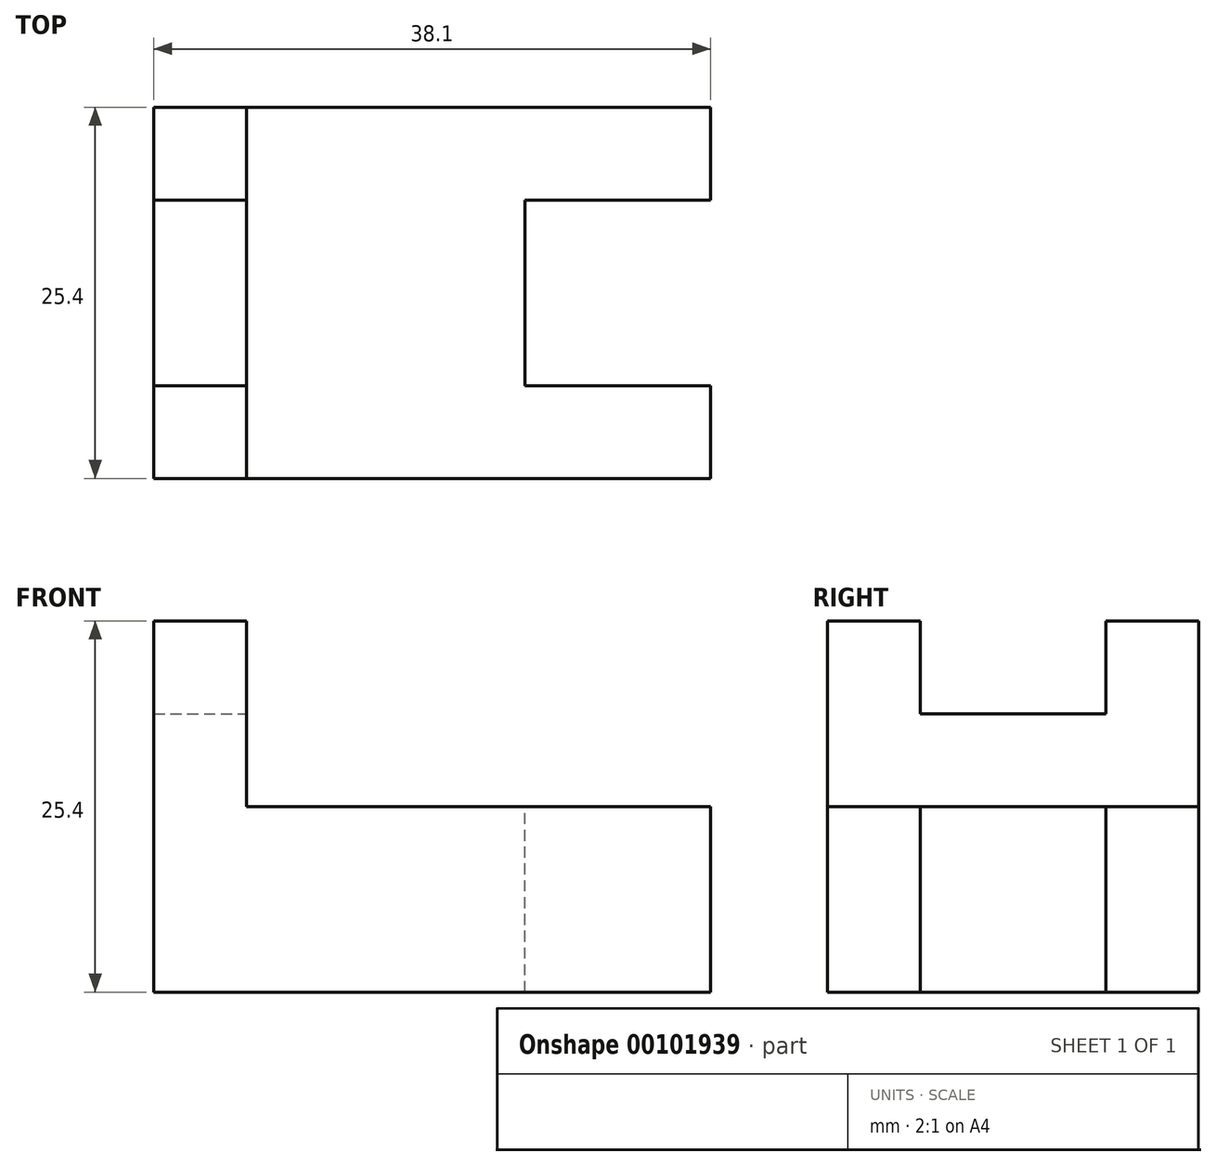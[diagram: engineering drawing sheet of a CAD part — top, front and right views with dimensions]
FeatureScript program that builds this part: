
annotation { "Feature Type Name" : "Feature", "Feature Type Description" : "" }
export const myFeature = defineFeature(function(context is Context, id is Id, definition is map)
    precondition{}
    {
        {
            var Q0;
            Q0=qCreatedBy(makeId("Front.planeOp"),FACE);
            var sketch = newSketch(context, id + "F0", { "sketchPlane" : qUnion([Q0])});
            skLineSegment(sketch, "E0", {"start": v(0, 0) * mm, "end": v(38.1, 0) * mm});
            skLineSegment(sketch, "E1", {"start": v(38.1, 0) * mm, "end": v(38.1, 12.7) * mm});
            skLineSegment(sketch, "E2", {"start": v(38.1, 12.7) * mm, "end": v(6.35, 12.7) * mm});
            skLineSegment(sketch, "E3", {"start": v(6.35, 12.7) * mm, "end": v(6.35, 25.4) * mm});
            skLineSegment(sketch, "E4", {"start": v(6.35, 25.4) * mm, "end": v(0, 25.4) * mm});
            skLineSegment(sketch, "E5", {"start": v(0, 25.4) * mm, "end": v(0, 0) * mm});
            skSolve(sketch);
        }
        {
            var Q0;
            Q0 = qSketchRegion(id + "F0", true);
            extrude(context, id + "F1", {"entities" : qUnion([Q0]), "endBound" : BoundingType.SYMMETRIC, "depth" : 25.4 * mm});
        }
        {
            var Q0;
            Q0=makeQuery(id+"F1.opExtrude","SWEPT_FACE",FACE,{"disambiguationData":[OSD([sQuery(id+"F0.wireOp",EDGE,"E3")])]});
            var sketch = newSketch(context, id + "F2", { "sketchPlane" : qUnion([Q0])});
            skLineSegment(sketch, "E6.bottom", {"start": v(-6.35, 25.4) * mm, "end": v(6.35, 25.4) * mm});
            skLineSegment(sketch, "E6.top", {"start": v(-6.35, 19.05) * mm, "end": v(6.35, 19.05) * mm});
            skLineSegment(sketch, "E6.left", {"start": v(-6.35, 25.4) * mm, "end": v(-6.35, 19.05) * mm});
            skLineSegment(sketch, "E6.right", {"start": v(6.35, 25.4) * mm, "end": v(6.35, 19.05) * mm});
            skSolve(sketch);
        }
        {
            var Q0;
            Q0=makeQuery(id+"F2.imprint","IMPRINT",FACE,{"disambiguationData":[TD([[makeQuery(id+"F2.imprint","IMPRINT",EDGE,{"derivedFrom":sQuery(id+"F2.wireOp",EDGE,"E6.bottom")}),-1.0]])]});
            extrude(context, id + "F3", {"entities" : qUnion([Q0]), "operationType" : NewBodyOperationType.REMOVE, "endBound" : BoundingType.THROUGH_ALL, "oppositeDirection" : true, "depth" : 25.4 * mm});
        }
        {
            var Q0;
            Q0=makeQuery(id+"F1.opExtrude","SWEPT_FACE",FACE,{"disambiguationData":[OSD([sQuery(id+"F0.wireOp",EDGE,"E2")])]});
            var sketch = newSketch(context, id + "F4", { "sketchPlane" : qUnion([Q0])});
            skLineSegment(sketch, "E7.bottom", {"start": v(38.1, 6.35) * mm, "end": v(25.4, 6.35) * mm});
            skLineSegment(sketch, "E7.top", {"start": v(38.1, -6.35) * mm, "end": v(25.4, -6.35) * mm});
            skLineSegment(sketch, "E7.left", {"start": v(38.1, 6.35) * mm, "end": v(38.1, -6.35) * mm});
            skLineSegment(sketch, "E7.right", {"start": v(25.4, 6.35) * mm, "end": v(25.4, -6.35) * mm});
            skSolve(sketch);
        }
        {
            var Q0;
            Q0=makeQuery(id+"F4.imprint","IMPRINT",FACE,{"disambiguationData":[TD([[makeQuery(id+"F4.imprint","IMPRINT",EDGE,{"derivedFrom":sQuery(id+"F4.wireOp",EDGE,"E7.bottom")}),1.0]])]});
            extrude(context, id + "F5", {"entities" : qUnion([Q0]), "operationType" : NewBodyOperationType.REMOVE, "endBound" : BoundingType.THROUGH_ALL, "oppositeDirection" : true, "depth" : 25.4 * mm});
        }
    });
